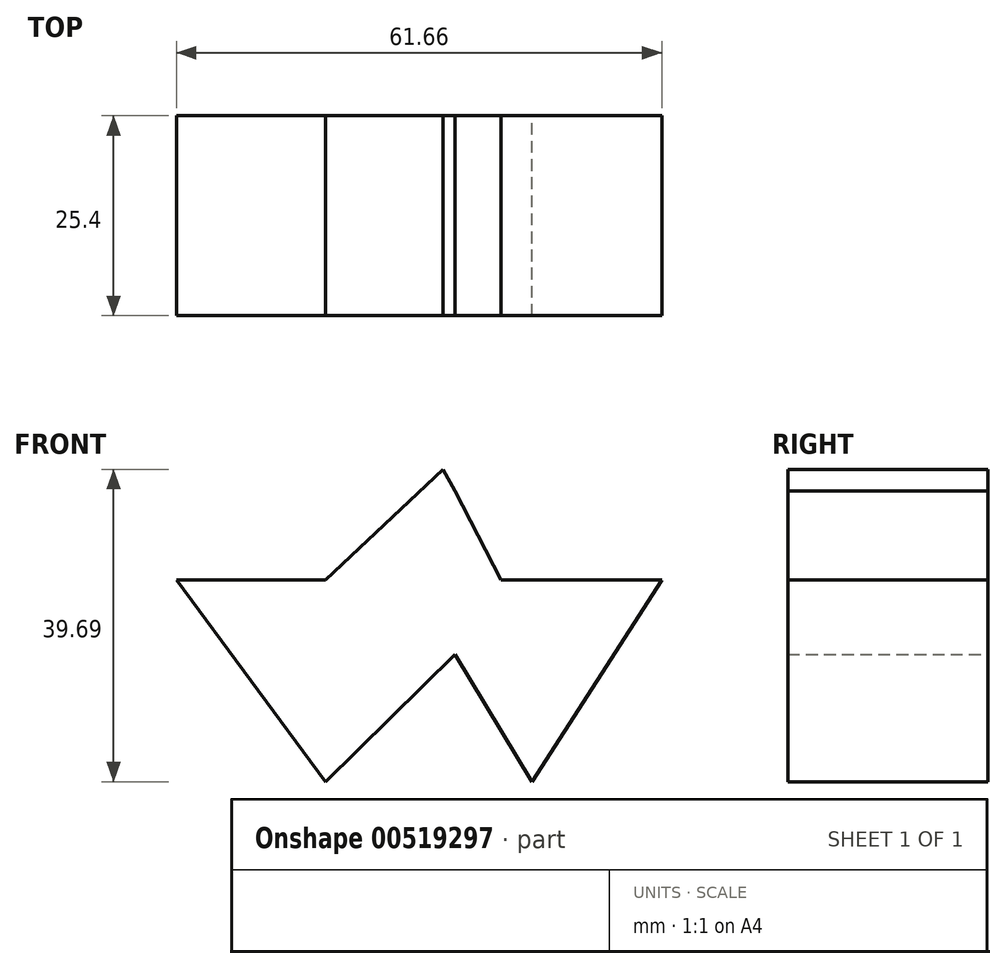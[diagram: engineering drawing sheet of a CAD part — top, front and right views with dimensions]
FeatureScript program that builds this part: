
annotation { "Feature Type Name" : "Feature", "Feature Type Description" : "" }
export const myFeature = defineFeature(function(context is Context, id is Id, definition is map)
    precondition{}
    {
        {
            var Q0;
            Q0=qCreatedBy(makeId("Front.planeOp"),FACE);
            var sketch = newSketch(context, id + "F0", { "sketchPlane" : qUnion([Q0])});
            skLineSegment(sketch, "E0", {"start": v(-36.33, 61.36) * mm, "end": v(-51.28, 47.32) * mm});
            skLineSegment(sketch, "E1", {"start": v(-51.28, 47.32) * mm, "end": v(-70.21, 47.32) * mm});
            skLineSegment(sketch, "E2", {"start": v(-70.21, 47.32) * mm, "end": v(-51.28, 21.67) * mm});
            skLineSegment(sketch, "E3", {"start": v(-51.28, 21.67) * mm, "end": v(-34.8, 37.85) * mm});
            skLineSegment(sketch, "E4", {"start": v(-34.8, 37.85) * mm, "end": v(-25.03, 21.67) * mm});
            skLineSegment(sketch, "E5", {"start": v(-25.03, 21.67) * mm, "end": v(-8.55, 47.32) * mm});
            skLineSegment(sketch, "E6", {"start": v(-8.55, 47.32) * mm, "end": v(-29, 47.32) * mm});
            skLineSegment(sketch, "E7", {"start": v(-29, 47.32) * mm, "end": v(-34.8, 58.61) * mm});
            skLineSegment(sketch, "E8", {"start": v(-34.8, 58.61) * mm, "end": v(-36.33, 61.36) * mm});
            skSolve(sketch);
        }
        {
            var Q0;
            Q0=makeQuery(id+"F0.imprint","IMPRINT",FACE,{"disambiguationData":[TD([[makeQuery(id+"F0.imprint","IMPRINT",EDGE,{"derivedFrom":sQuery(id+"F0.wireOp",EDGE,"E0")}),1.0]])]});
            extrude(context, id + "F1", {"entities" : qUnion([Q0]), "depth" : 25.4 * mm, "offsetDistance" : 25.4 * mm});
        }
    });
